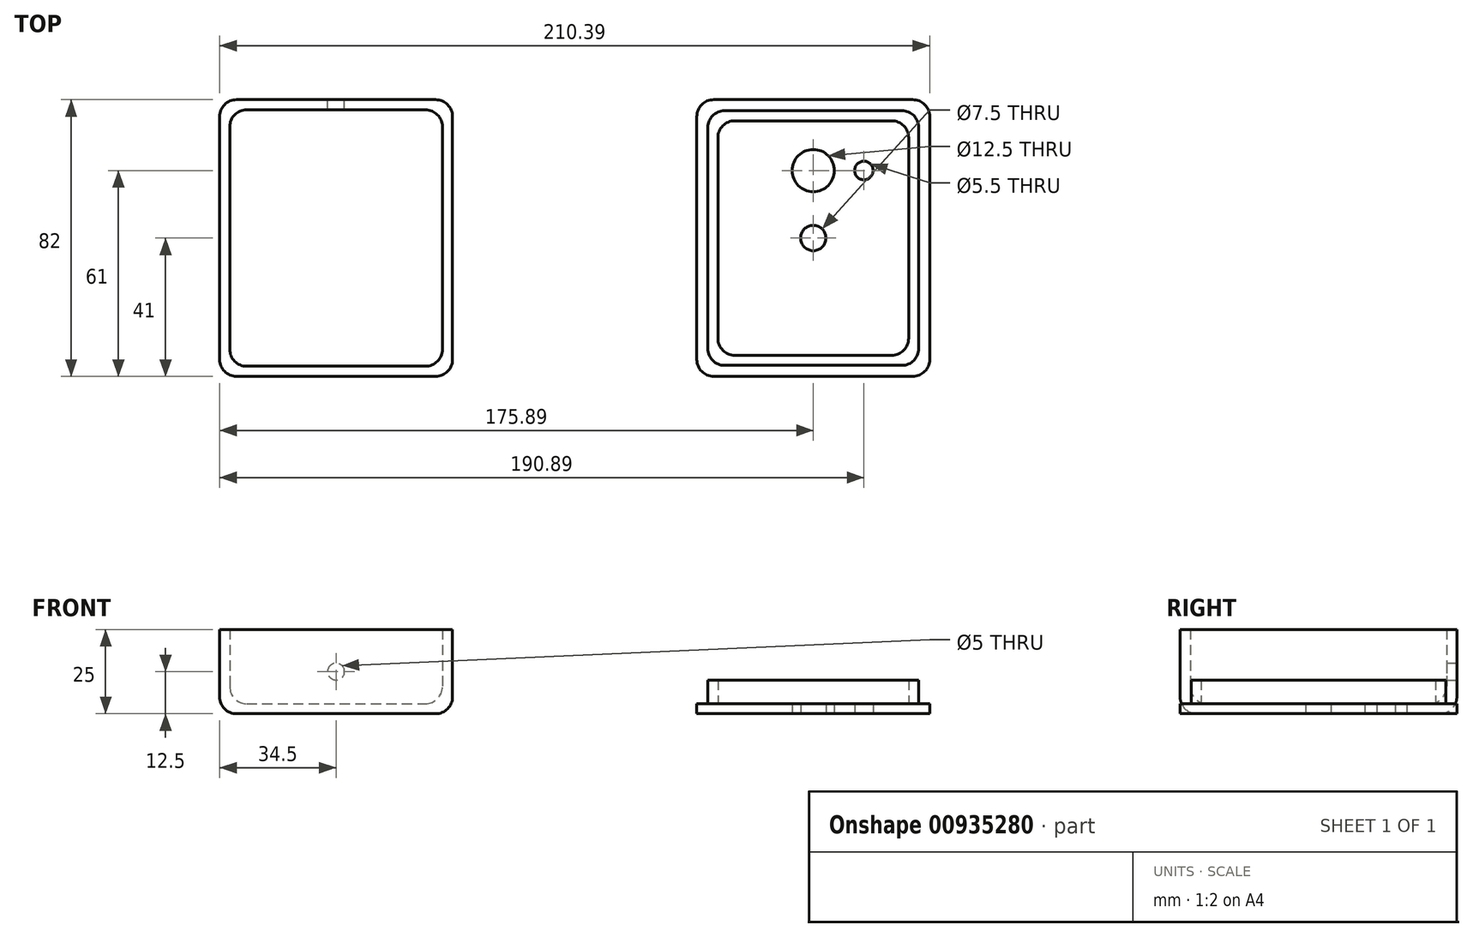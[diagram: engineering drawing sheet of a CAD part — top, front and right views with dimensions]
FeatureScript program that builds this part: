
annotation { "Feature Type Name" : "Feature", "Feature Type Description" : "" }
export const myFeature = defineFeature(function(context is Context, id is Id, definition is map)
    precondition{}
    {
        {
            var Q0;
            Q0=qCreatedBy(makeId("Top.planeOp"),FACE);
            var sketch = newSketch(context, id + "F0", { "sketchPlane" : qUnion([Q0])});
            skLineSegment(sketch, "E0.bottom", {"start": v(-34.5, 41) * mm, "end": v(34.5, 41) * mm});
            skLineSegment(sketch, "E0.top", {"start": v(-34.5, -41) * mm, "end": v(34.5, -41) * mm});
            skLineSegment(sketch, "E0.left", {"start": v(-34.5, 41) * mm, "end": v(-34.5, -41) * mm});
            skLineSegment(sketch, "E0.right", {"start": v(34.5, 41) * mm, "end": v(34.5, -41) * mm});
            skPoint(sketch, "E0.middle", {"position": v(0, 0) * mm});
            skLineSegment(sketch, "E1.0", {"start": v(-31.5, 38) * mm, "end": v(31.5, 38) * mm});
            skLineSegment(sketch, "E1.1", {"start": v(-31.5, 38) * mm, "end": v(-31.5, -38) * mm});
            skLineSegment(sketch, "E1.2", {"start": v(-31.5, -38) * mm, "end": v(31.5, -38) * mm});
            skLineSegment(sketch, "E1.3", {"start": v(31.5, 38) * mm, "end": v(31.5, -38) * mm});
            skLineSegment(sketch, "E2.bottom", {"start": v(172.64, 37.75) * mm, "end": v(110.14, 37.75) * mm});
            skLineSegment(sketch, "E2.top", {"start": v(172.64, -37.75) * mm, "end": v(110.14, -37.75) * mm});
            skLineSegment(sketch, "E2.left", {"start": v(172.64, 37.75) * mm, "end": v(172.64, -37.75) * mm});
            skLineSegment(sketch, "E2.right", {"start": v(110.14, 37.75) * mm, "end": v(110.14, -37.75) * mm});
            skPoint(sketch, "E2.middle", {"position": v(141.39, 0) * mm});
            skLineSegment(sketch, "E3.0", {"start": v(169.64, 34.75) * mm, "end": v(169.64, -34.75) * mm});
            skLineSegment(sketch, "E3.1", {"start": v(169.64, 34.75) * mm, "end": v(113.14, 34.75) * mm});
            skLineSegment(sketch, "E3.2", {"start": v(113.14, 34.75) * mm, "end": v(113.14, -34.75) * mm});
            skLineSegment(sketch, "E3.3", {"start": v(169.64, -34.75) * mm, "end": v(113.14, -34.75) * mm});
            skCircle(sketch, "E4", {"center": v(141.39, 20) * mm, "radius": 6.25 * mm});
            skCircle(sketch, "E5", {"center": v(141.39, 0) * mm, "radius": 3.75 * mm});
            skCircle(sketch, "E6", {"center": v(156.39, 20) * mm, "radius": 2.75 * mm});
            skLineSegment(sketch, "E7.bottom", {"start": v(106.89, -41) * mm, "end": v(175.89, -41) * mm});
            skLineSegment(sketch, "E7.top", {"start": v(106.89, 41) * mm, "end": v(175.89, 41) * mm});
            skLineSegment(sketch, "E7.left", {"start": v(106.89, -41) * mm, "end": v(106.89, 41) * mm});
            skLineSegment(sketch, "E7.right", {"start": v(175.89, -41) * mm, "end": v(175.89, 41) * mm});
            skSolve(sketch);
        }
        {
            var Q0;
            Q0=makeQuery(id+"F0.imprint","IMPRINT",FACE,{"disambiguationData":[TD([[makeQuery(id+"F0.imprint","IMPRINT",EDGE,{"derivedFrom":sQuery(id+"F0.wireOp",EDGE,"E0.bottom")}),-1.0]])]});
            extrude(context, id + "F1", {"entities" : qUnion([Q0]), "depth" : 25 * mm, "offsetDistance" : 25 * mm});
        }
        {
            var Q0;
            Q0=makeQuery(id+"F0.imprint","IMPRINT",FACE,{"disambiguationData":[TD([[makeQuery(id+"F0.imprint","IMPRINT",EDGE,{"derivedFrom":sQuery(id+"F0.wireOp",EDGE,"E1.0")}),-1.0]])]});
            extrude(context, id + "F2", {"entities" : qUnion([Q0]), "operationType" : NewBodyOperationType.ADD, "depth" : 3 * mm, "offsetDistance" : 25 * mm});
        }
        {
            var Q0;
            Q0=makeQuery(id+"F0.imprint","IMPRINT",FACE,{"disambiguationData":[TD([[makeQuery(id+"F0.imprint","IMPRINT",EDGE,{"derivedFrom":sQuery(id+"F0.wireOp",EDGE,"E2.bottom")}),1.0]])]});
            extrude(context, id + "F3", {"entities" : qUnion([Q0]), "depth" : 10 * mm, "offsetDistance" : 25 * mm});
        }
        {
            var Q0;
            Q0=makeQuery(id+"F0.imprint","IMPRINT",FACE,{"disambiguationData":[TD([[makeQuery(id+"F0.imprint","IMPRINT",EDGE,{"derivedFrom":sQuery(id+"F0.wireOp",EDGE,"E2.bottom")}),-1.0]])]});
            var Q1;
            Q1=makeQuery(id+"F0.imprint","IMPRINT",FACE,{"disambiguationData":[TD([[makeQuery(id+"F0.imprint","IMPRINT",EDGE,{"derivedFrom":sQuery(id+"F0.wireOp",EDGE,"E3.0")}),-1.0]])]});
            extrude(context, id + "F4", {"entities" : qUnion([Q0, Q1]), "operationType" : NewBodyOperationType.ADD, "depth" : 3 * mm, "offsetDistance" : 25 * mm});
        }
        {
            var Q0;
            Q0=makeQuery(id+"F1.opExtrude","SWEPT_EDGE",EDGE,{"disambiguationData":[OSD([sQuery(id+"F0.wireOp",EDGE,"E0.bottom"),sQuery(id+"F0.wireOp",EDGE,"E0.right")])]});
            var Q1;
            Q1=makeQuery(id+"F1.opExtrude","SWEPT_EDGE",EDGE,{"disambiguationData":[OSD([sQuery(id+"F0.wireOp",EDGE,"E1.0"),sQuery(id+"F0.wireOp",EDGE,"E1.3")])]});
            var Q2;
            Q2=makeQuery(id+"F1.opExtrude","SWEPT_EDGE",EDGE,{"disambiguationData":[OSD([sQuery(id+"F0.wireOp",EDGE,"E1.0"),sQuery(id+"F0.wireOp",EDGE,"E1.1")])]});
            var Q3;
            Q3=makeQuery(id+"F1.opExtrude","SWEPT_EDGE",EDGE,{"disambiguationData":[OSD([sQuery(id+"F0.wireOp",EDGE,"E0.bottom"),sQuery(id+"F0.wireOp",EDGE,"E0.left")])]});
            var Q4;
            Q4=makeQuery(id+"F1.opExtrude","SWEPT_EDGE",EDGE,{"disambiguationData":[OSD([sQuery(id+"F0.wireOp",EDGE,"E0.top"),sQuery(id+"F0.wireOp",EDGE,"E0.right")])]});
            var Q5;
            Q5=makeQuery(id+"F1.opExtrude","SWEPT_EDGE",EDGE,{"disambiguationData":[OSD([sQuery(id+"F0.wireOp",EDGE,"E1.2"),sQuery(id+"F0.wireOp",EDGE,"E1.3")])]});
            var Q6;
            Q6=makeQuery(id+"F1.opExtrude","SWEPT_EDGE",EDGE,{"disambiguationData":[OSD([sQuery(id+"F0.wireOp",EDGE,"E0.top"),sQuery(id+"F0.wireOp",EDGE,"E0.left")])]});
            var Q7;
            Q7=makeQuery(id+"F1.opExtrude","SWEPT_EDGE",EDGE,{"disambiguationData":[OSD([sQuery(id+"F0.wireOp",EDGE,"E1.1"),sQuery(id+"F0.wireOp",EDGE,"E1.2")])]});
            var Q8;
            {var subQ0=sQuery(id+"F0.wireOp",EDGE,"E1.3");var subQ1=sQuery(id+"F0.wireOp",EDGE,"E1.2");var subQ2=sQuery(id+"F0.wireOp",EDGE,"E1.1");var subQ3=sQuery(id+"F0.wireOp",EDGE,"E1.0");Q8=makeQuery(id+"F2.boolean.opBoolean","MERGE",FACE,{"derivedFrom":[makeQuery(id+"F1.opExtrude","CAP_FACE",FACE,{"disambiguationData":[OSD([sQuery(id+"F0.wireOp",EDGE,"E0.bottom"),sQuery(id+"F0.wireOp",EDGE,"E0.top"),sQuery(id+"F0.wireOp",EDGE,"E0.left"),sQuery(id+"F0.wireOp",EDGE,"E0.right"),subQ3,subQ2,subQ1,subQ0])],"isStart":true}),makeQuery(id+"F2.opExtrude","CAP_FACE",FACE,{"disambiguationData":[OSD([subQ3,subQ2,subQ1,subQ0])],"isStart":true})]});}
            var Q9;
            Q9=makeQuery(id+"F2.opExtrude","CAP_FACE",FACE,{"disambiguationData":[OSD([sQuery(id+"F0.wireOp",EDGE,"E1.0"),sQuery(id+"F0.wireOp",EDGE,"E1.1"),sQuery(id+"F0.wireOp",EDGE,"E1.2"),sQuery(id+"F0.wireOp",EDGE,"E1.3")])],"isStart":false});
            var Q10;
            Q10=makeQuery(id+"F4.opExtrude","SWEPT_EDGE",EDGE,{"disambiguationData":[OSD([sQuery(id+"F0.wireOp",EDGE,"E7.bottom"),sQuery(id+"F0.wireOp",EDGE,"E7.left")])]});
            var Q11;
            Q11=makeQuery(id+"F3.opExtrude","SWEPT_EDGE",EDGE,{"disambiguationData":[OSD([sQuery(id+"F0.wireOp",EDGE,"E2.top"),sQuery(id+"F0.wireOp",EDGE,"E2.left")])]});
            var Q12;
            Q12=makeQuery(id+"F3.opExtrude","SWEPT_EDGE",EDGE,{"disambiguationData":[OSD([sQuery(id+"F0.wireOp",EDGE,"E2.bottom"),sQuery(id+"F0.wireOp",EDGE,"E2.left")])]});
            var Q13;
            Q13=makeQuery(id+"F3.opExtrude","SWEPT_EDGE",EDGE,{"disambiguationData":[OSD([sQuery(id+"F0.wireOp",EDGE,"E2.bottom"),sQuery(id+"F0.wireOp",EDGE,"E2.right")])]});
            var Q14;
            Q14=makeQuery(id+"F3.opExtrude","SWEPT_EDGE",EDGE,{"disambiguationData":[OSD([sQuery(id+"F0.wireOp",EDGE,"E3.0"),sQuery(id+"F0.wireOp",EDGE,"E3.1")])]});
            var Q15;
            Q15=makeQuery(id+"F3.opExtrude","SWEPT_EDGE",EDGE,{"disambiguationData":[OSD([sQuery(id+"F0.wireOp",EDGE,"E3.1"),sQuery(id+"F0.wireOp",EDGE,"E3.2")])]});
            var Q16;
            Q16=makeQuery(id+"F3.opExtrude","SWEPT_EDGE",EDGE,{"disambiguationData":[OSD([sQuery(id+"F0.wireOp",EDGE,"E3.0"),sQuery(id+"F0.wireOp",EDGE,"E3.3")])]});
            var Q17;
            Q17=makeQuery(id+"F3.opExtrude","SWEPT_EDGE",EDGE,{"disambiguationData":[OSD([sQuery(id+"F0.wireOp",EDGE,"E3.2"),sQuery(id+"F0.wireOp",EDGE,"E3.3")])]});
            var Q18;
            Q18=makeQuery(id+"F4.opExtrude","SWEPT_EDGE",EDGE,{"disambiguationData":[OSD([sQuery(id+"F0.wireOp",EDGE,"E7.top"),sQuery(id+"F0.wireOp",EDGE,"E7.right")])]});
            var Q19;
            Q19=makeQuery(id+"F4.opExtrude","SWEPT_EDGE",EDGE,{"disambiguationData":[OSD([sQuery(id+"F0.wireOp",EDGE,"E7.bottom"),sQuery(id+"F0.wireOp",EDGE,"E7.right")])]});
            var Q20;
            Q20=makeQuery(id+"F4.opExtrude","SWEPT_EDGE",EDGE,{"disambiguationData":[OSD([sQuery(id+"F0.wireOp",EDGE,"E7.top"),sQuery(id+"F0.wireOp",EDGE,"E7.left")])]});
            var Q21;
            Q21=makeQuery(id+"F3.opExtrude","SWEPT_EDGE",EDGE,{"disambiguationData":[OSD([sQuery(id+"F0.wireOp",EDGE,"E2.top"),sQuery(id+"F0.wireOp",EDGE,"E2.right")])]});
            fillet(context, id + "F5", {"entities" : qUnion([Q0, Q1, Q2, Q3, Q4, Q5, Q6, Q7, Q8, Q9, Q10, Q11, Q12, Q13, Q14, Q15, Q16, Q17, Q18, Q19, Q20, Q21]), "radius" : 5 * mm, "tangentPropagation" : true, "allowEdgeOverflow" : false});
        }
        {
            var Q0;
            Q0=makeQuery(id+"F1.opExtrude","SWEPT_FACE",FACE,{"disambiguationData":[OSD([sQuery(id+"F0.wireOp",EDGE,"E0.bottom")])]});
            var sketch = newSketch(context, id + "F6", { "sketchPlane" : qUnion([Q0])});
            skCircle(sketch, "E8", {"center": v(0, 12.5) * mm, "radius": 2.5 * mm});
            skSolve(sketch);
        }
        {
            var Q0;
            Q0=makeQuery(id+"F6.imprint","IMPRINT",FACE,{"disambiguationData":[TD([[makeQuery(id+"F6.imprint","IMPRINT",EDGE,{"derivedFrom":sQuery(id+"F6.wireOp",EDGE,"E8")}),1.0]])]});
            extrude(context, id + "F7", {"entities" : qUnion([Q0]), "operationType" : NewBodyOperationType.REMOVE, "oppositeDirection" : true, "depth" : 25 * mm, "offsetDistance" : 25 * mm});
        }
    });
